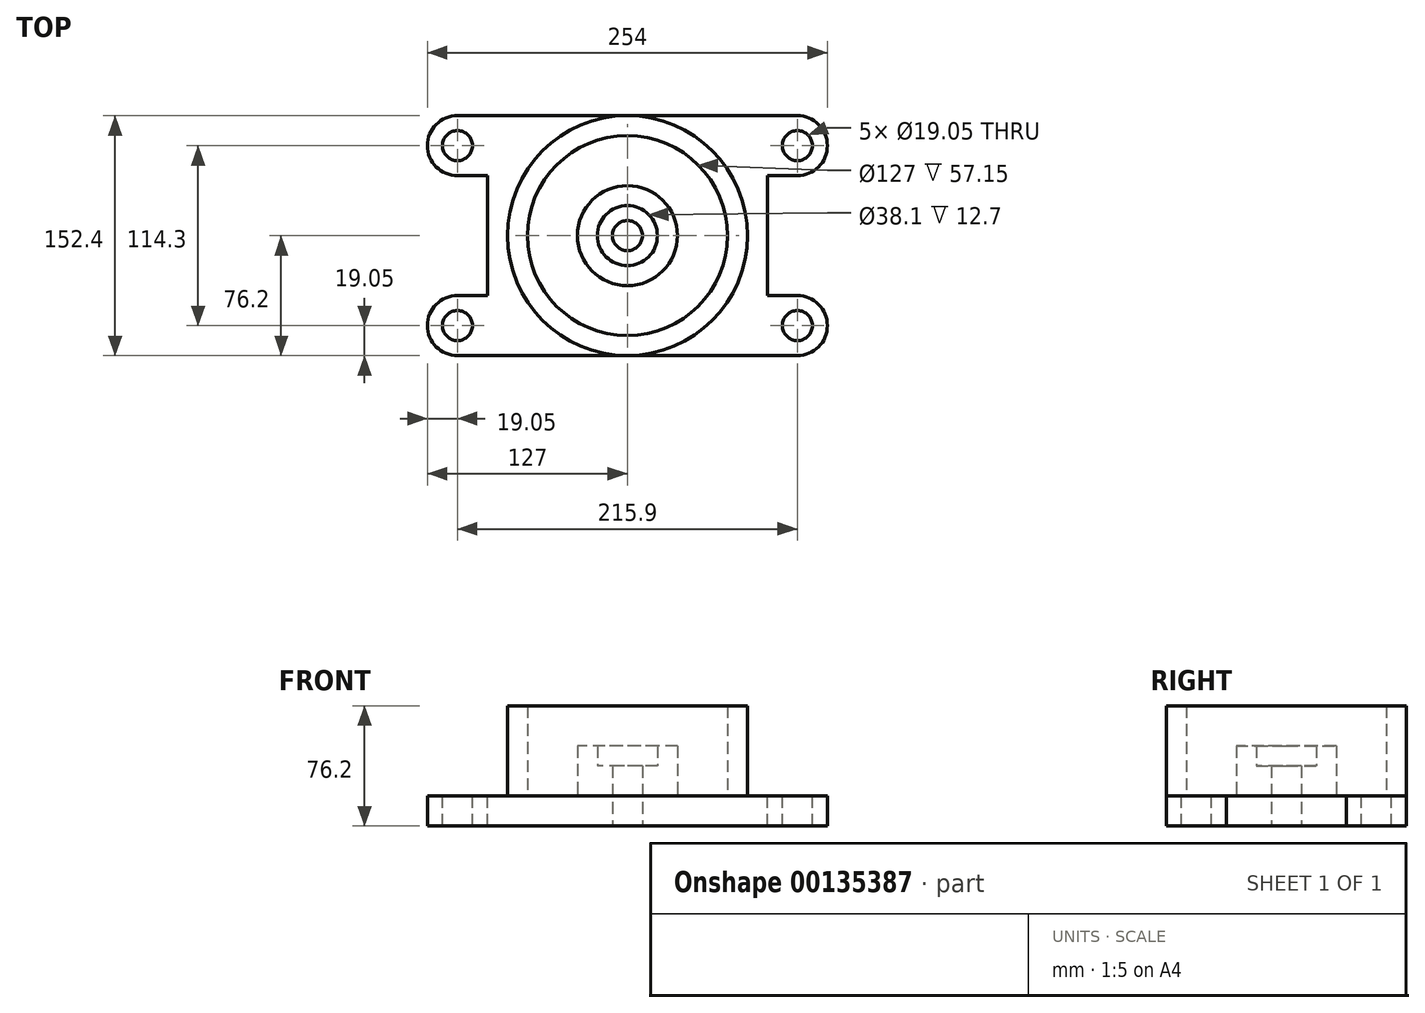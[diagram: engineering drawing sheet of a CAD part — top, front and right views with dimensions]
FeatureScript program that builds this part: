
annotation { "Feature Type Name" : "Feature", "Feature Type Description" : "" }
export const myFeature = defineFeature(function(context is Context, id is Id, definition is map)
    precondition{}
    {
        {
            var Q0;
            Q0=qCreatedBy(makeId("Top.planeOp"),FACE);
            var sketch = newSketch(context, id + "F0", { "sketchPlane" : qUnion([Q0])});
            skCircle(sketch, "E0", {"center": v(0, 0) * mm, "radius": 76.2 * mm});
            skCircle(sketch, "E1", {"center": v(0, 0) * mm, "radius": 63.5 * mm});
            skCircle(sketch, "E2", {"center": v(0, 0) * mm, "radius": 19.05 * mm});
            skCircle(sketch, "E3", {"center": v(0, 0) * mm, "radius": 31.75 * mm});
            skLineSegment(sketch, "E4", {"start": v(-88.9, 76.2) * mm, "end": v(88.9, 76.2) * mm});
            skLineSegment(sketch, "E5", {"start": v(88.9, -76.2) * mm, "end": v(-88.9, -76.2) * mm});
            skLineSegment(sketch, "E6", {"start": v(-88.9, 76.2) * mm, "end": v(-88.9, -76.2) * mm});
            skLineSegment(sketch, "E7", {"start": v(88.9, 76.2) * mm, "end": v(88.9, -76.2) * mm});
            skLineSegment(sketch, "E8.bottom", {"start": v(88.9, 76.2) * mm, "end": v(107.95, 76.2) * mm});
            skLineSegment(sketch, "E8.top", {"start": v(88.9, 38.1) * mm, "end": v(107.95, 38.1) * mm});
            skLineSegment(sketch, "E8.right", {"start": v(127, 57.15) * mm, "end": v(127, 57.15) * mm});
            skPoint(sketch, "E9.visualSharp", {"position": v(127, 76.2) * mm});
            skArc(sketch, "E9.filletArc", {"start": v(127, 57.15) * mm, "mid": v(121.42, 70.62) * mm, "end": v(107.95, 76.2) * mm});
            skPoint(sketch, "E10.visualSharp", {"position": v(127, 38.1) * mm});
            skArc(sketch, "E10.filletArc", {"start": v(107.95, 38.1) * mm, "mid": v(121.42, 43.68) * mm, "end": v(127, 57.15) * mm});
            skCircle(sketch, "E11", {"center": v(107.95, 57.15) * mm, "radius": 9.53 * mm});
            skArc(sketch, "E12.MirrorCS", {"start": v(107.95, -38.1) * mm, "mid": v(121.42, -43.68) * mm, "end": v(127, -57.15) * mm});
            skCircle(sketch, "E13.MirrorC", {"center": v(107.95, -57.15) * mm, "radius": 9.53 * mm});
            skArc(sketch, "E14.MirrorCS", {"start": v(127, -57.15) * mm, "mid": v(121.42, -70.62) * mm, "end": v(107.95, -76.2) * mm});
            skLineSegment(sketch, "E15.MirrorCS", {"start": v(88.9, -38.1) * mm, "end": v(107.95, -38.1) * mm});
            skLineSegment(sketch, "E16.MirrorCS", {"start": v(88.9, -76.2) * mm, "end": v(107.95, -76.2) * mm});
            skArc(sketch, "E17.MirrorCS", {"start": v(-107.95, -38.1) * mm, "mid": v(-121.42, -43.68) * mm, "end": v(-127, -57.15) * mm});
            skArc(sketch, "E18.MirrorCS", {"start": v(-127, -57.15) * mm, "mid": v(-121.42, -70.62) * mm, "end": v(-107.95, -76.2) * mm});
            skLineSegment(sketch, "E19.MirrorCS", {"start": v(-88.9, -76.2) * mm, "end": v(-107.95, -76.2) * mm});
            skLineSegment(sketch, "E20.MirrorCS", {"start": v(-88.9, -38.1) * mm, "end": v(-107.95, -38.1) * mm});
            skCircle(sketch, "E21.MirrorC", {"center": v(-107.95, -57.15) * mm, "radius": 9.53 * mm});
            skArc(sketch, "E22.MirrorCS", {"start": v(-127, 57.15) * mm, "mid": v(-121.42, 70.62) * mm, "end": v(-107.95, 76.2) * mm});
            skCircle(sketch, "E23.MirrorC", {"center": v(-107.95, 57.15) * mm, "radius": 9.53 * mm});
            skArc(sketch, "E24.MirrorCS", {"start": v(-107.95, 38.1) * mm, "mid": v(-121.42, 43.68) * mm, "end": v(-127, 57.15) * mm});
            skLineSegment(sketch, "E25.MirrorCS", {"start": v(-88.9, 38.1) * mm, "end": v(-107.95, 38.1) * mm});
            skLineSegment(sketch, "E26.MirrorCS", {"start": v(-88.9, 76.2) * mm, "end": v(-107.95, 76.2) * mm});
            skLineSegment(sketch, "E27", {"start": v(-88.9, 76.2) * mm, "end": v(-88.9, 38.1) * mm});
            skLineSegment(sketch, "E28", {"start": v(88.9, -38.1) * mm, "end": v(88.9, -76.2) * mm});
            skLineSegment(sketch, "E29", {"start": v(107.95, -76.2) * mm, "end": v(88.9, -76.2) * mm});
            skCircle(sketch, "E30", {"center": v(0, 0) * mm, "radius": 9.53 * mm});
            skSolve(sketch);
        }
        {
            var Q0;
            Q0 = qSketchRegion(id + "F0", true);
            var Q1;
            Q1=makeQuery(id+"F0.imprint","IMPRINT",FACE,{"disambiguationData":[TD([[makeQuery(id+"F0.imprint","IMPRINT",EDGE,{"derivedFrom":sQuery(id+"F0.wireOp",EDGE,"E1")}),1.0]])]});
            var Q2;
            Q2=makeQuery(id+"F0.imprint","IMPRINT",FACE,{"disambiguationData":[TD([[makeQuery(id+"F0.imprint","IMPRINT",EDGE,{"derivedFrom":sQuery(id+"F0.wireOp",EDGE,"E2")}),-1.0]])]});
            var Q3;
            Q3=makeQuery(id+"F0.imprint","IMPRINT",FACE,{"disambiguationData":[TD([[makeQuery(id+"F0.imprint","IMPRINT",EDGE,{"derivedFrom":sQuery(id+"F0.wireOp",EDGE,"E2")}),1.0]])]});
            var Q4;
            Q4=makeQuery(id+"F0.imprint","IMPRINT",FACE,{"disambiguationData":[TD([[makeQuery(id+"F0.imprint","IMPRINT",EDGE,{"derivedFrom":sQuery(id+"F0.wireOp",EDGE,"E30")}),1.0]])]});
            extrude(context, id + "F1", {"entities" : qUnion([Q0, Q1, Q2, Q3, Q4]), "oppositeDirection" : true, "depth" : 19.05 * mm});
        }
        {
            var Q0;
            Q0=makeQuery(id+"F0.imprint","IMPRINT",FACE,{"disambiguationData":[TD([[makeQuery(id+"F0.imprint","IMPRINT",EDGE,{"derivedFrom":sQuery(id+"F0.wireOp",EDGE,"E1")}),-1.0]])]});
            extrude(context, id + "F2", {"entities" : qUnion([Q0]), "operationType" : NewBodyOperationType.ADD, "depth" : 57.15 * mm});
        }
        {
            var Q0;
            Q0=makeQuery(id+"F0.imprint","IMPRINT",FACE,{"disambiguationData":[TD([[makeQuery(id+"F0.imprint","IMPRINT",EDGE,{"derivedFrom":sQuery(id+"F0.wireOp",EDGE,"E2")}),-1.0]])]});
            extrude(context, id + "F3", {"entities" : qUnion([Q0]), "operationType" : NewBodyOperationType.ADD, "depth" : 31.75 * mm});
        }
        {
            var Q0;
            Q0=makeQuery(id+"F0.imprint","IMPRINT",FACE,{"disambiguationData":[TD([[makeQuery(id+"F0.imprint","IMPRINT",EDGE,{"derivedFrom":sQuery(id+"F0.wireOp",EDGE,"E2")}),1.0]])]});
            extrude(context, id + "F4", {"entities" : qUnion([Q0]), "operationType" : NewBodyOperationType.ADD, "depth" : 19.05 * mm});
        }
        {
            var Q0;
            Q0=makeQuery(id+"F0.imprint","IMPRINT",FACE,{"disambiguationData":[TD([[makeQuery(id+"F0.imprint","IMPRINT",EDGE,{"derivedFrom":sQuery(id+"F0.wireOp",EDGE,"E30")}),1.0]])]});
            extrude(context, id + "F5", {"entities" : qUnion([Q0]), "operationType" : NewBodyOperationType.REMOVE, "oppositeDirection" : true, "depth" : 25.4 * mm});
        }
    });
